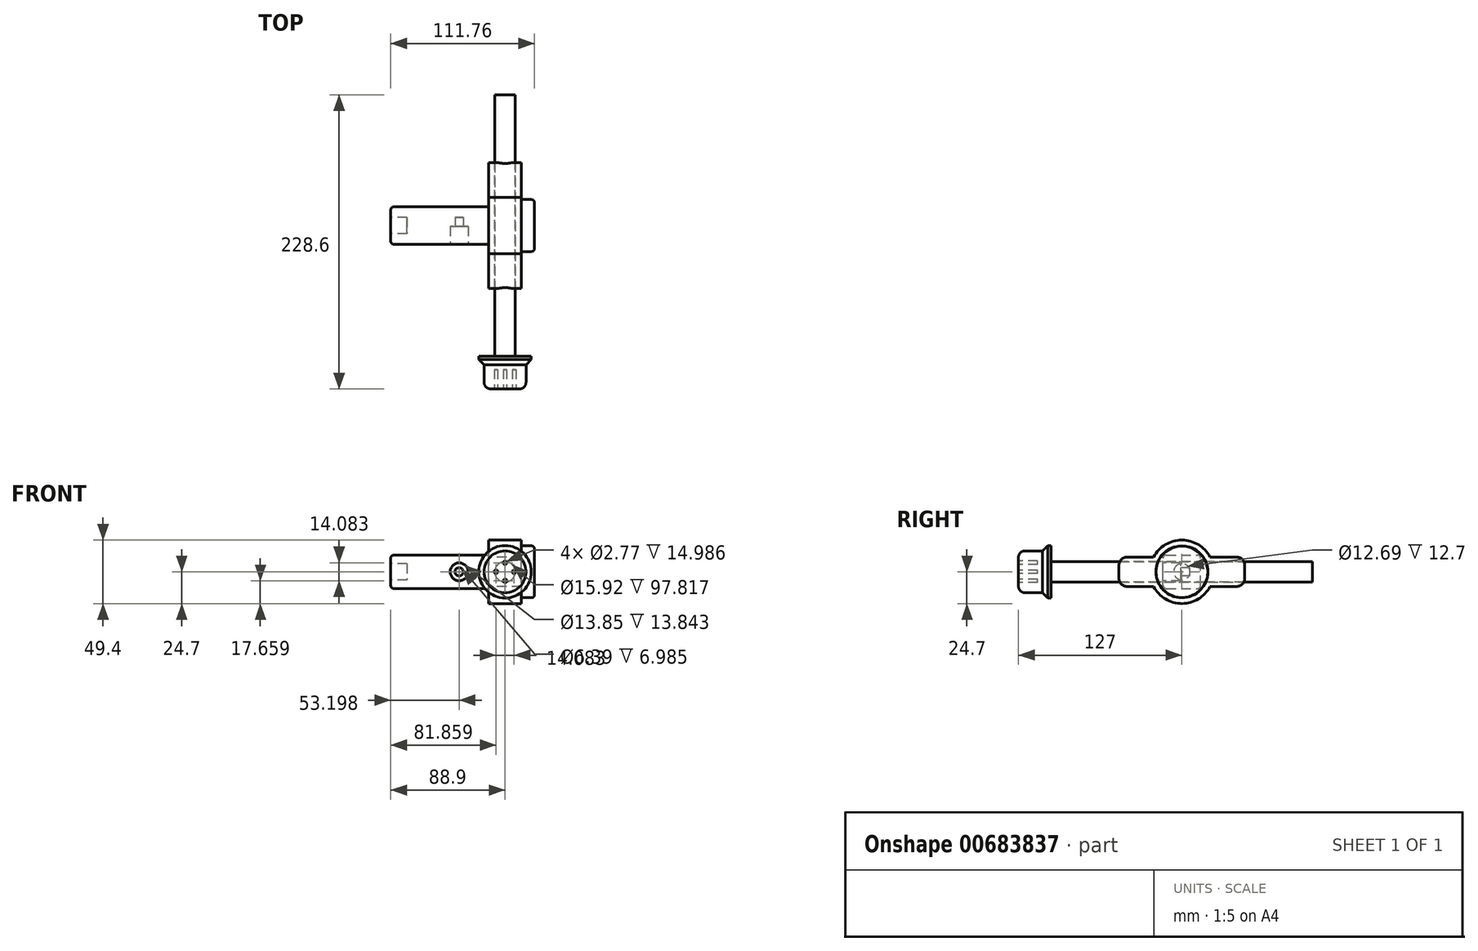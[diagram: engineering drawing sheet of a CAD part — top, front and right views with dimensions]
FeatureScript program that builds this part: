
annotation { "Feature Type Name" : "Feature", "Feature Type Description" : "" }
export const myFeature = defineFeature(function(context is Context, id is Id, definition is map)
    precondition{}
    {
        {
            var Q0;
            Q0=qCreatedBy(makeId("Right.planeOp"),FACE);
            var sketch = newSketch(context, id + "F0", { "sketchPlane" : qUnion([Q0])});
            skPoint(sketch, "E0.middle", {"position": v(0, 0) * mm});
            skPoint(sketch, "E0.left.end.orphan", {"position": v(25.79, 17.05) * mm});
            skPoint(sketch, "E0.bottom.start.orphan", {"position": v(25.79, -17.05) * mm});
            skPoint(sketch, "E0.right.start.orphan", {"position": v(-25.79, -17.05) * mm});
            skPoint(sketch, "E1.trimOffspring.end.orphan", {"position": v(-25.79, 17.05) * mm});
            skLineSegment(sketch, "E2.bottom", {"start": v(48.9, -11.44) * mm, "end": v(21.89, -11.44) * mm});
            skLineSegment(sketch, "E2.top", {"start": v(48.9, 11.44) * mm, "end": v(21.89, 11.44) * mm});
            skLineSegment(sketch, "E2.left", {"start": v(48.9, -11.44) * mm, "end": v(48.9, 11.44) * mm});
            skLineSegment(sketch, "E2.right", {"start": v(-48.9, -11.44) * mm, "end": v(-48.9, 11.44) * mm});
            skLineSegment(sketch, "E3.trimOffspring", {"start": v(-21.89, 11.44) * mm, "end": v(-48.9, 11.44) * mm});
            skLineSegment(sketch, "E4.trimOffspring", {"start": v(-21.89, -11.44) * mm, "end": v(-48.9, -11.44) * mm});
            skArc(sketch, "E5", {"start": v(21.89, 11.44) * mm, "mid": v(0, 24.7) * mm, "end": v(-21.89, 11.44) * mm});
            skArc(sketch, "E6.trimOffspring", {"start": v(-21.89, -11.44) * mm, "mid": v(0, -24.7) * mm, "end": v(21.89, -11.44) * mm});
            skSolve(sketch);
        }
        {
            var Q0;
            Q0=makeQuery(id+"F0.imprint","IMPRINT",FACE,{"disambiguationData":[TD([[makeQuery(id+"F0.imprint","IMPRINT",EDGE,{"derivedFrom":sQuery(id+"F0.wireOp",EDGE,"E2.bottom")}),-1.0]])]});
            extrude(context, id + "F1", {"entities" : qUnion([Q0]), "depth" : 12.7 * mm, "offsetDistance" : 25.4 * mm, "hasSecondDirection" : true, "secondDirectionOppositeDirection" : true, "secondDirectionDepth" : 12.7 * mm});
        }
        {
            var Q0;
            Q0=makeQuery(id+"F1.opExtrude","SWEPT_FACE",FACE,{"disambiguationData":[OSD([sQuery(id+"F0.wireOp",EDGE,"E2.right")])]});
            var sketch = newSketch(context, id + "F2", { "sketchPlane" : qUnion([Q0])});
            skCircle(sketch, "E7", {"center": v(0, 0) * mm, "radius": 7.96 * mm});
            skSolve(sketch);
        }
        {
            var Q0;
            Q0 = qSketchRegion(id + "F2", true);
            extrude(context, id + "F3", {"entities" : qUnion([Q0]), "operationType" : NewBodyOperationType.REMOVE, "oppositeDirection" : true, "depth" : 97.97 * mm, "offsetDistance" : 25.4 * mm});
        }
        {
            var Q0;
            Q0=qCreatedBy(makeId("Front.planeOp"),FACE);
            var sketch = newSketch(context, id + "F4", { "sketchPlane" : qUnion([Q0])});
            skCircle(sketch, "E8", {"center": v(0, 0) * mm, "radius": 7.96 * mm});
            skSolve(sketch);
        }
        {
            var Q0;
            Q0=makeQuery(id+"F4.imprint","IMPRINT",FACE,{"disambiguationData":[TD([[makeQuery(id+"F4.imprint","IMPRINT",EDGE,{"derivedFrom":sQuery(id+"F4.wireOp",EDGE,"E8")}),1.0]])]});
            extrude(context, id + "F5", {"entities" : qUnion([Q0]), "depth" : 101.6 * mm, "offsetDistance" : 25.4 * mm, "hasSecondDirection" : true, "secondDirectionOppositeDirection" : true, "secondDirectionDepth" : 101.6 * mm});
        }
        {
            var Q0;
            Q0=makeQuery(id+"F1.opExtrude","CAP_FACE",FACE,{"disambiguationData":[OSD([sQuery(id+"F0.wireOp",EDGE,"E2.bottom"),sQuery(id+"F0.wireOp",EDGE,"E2.top"),sQuery(id+"F0.wireOp",EDGE,"E2.left"),sQuery(id+"F0.wireOp",EDGE,"E2.right"),sQuery(id+"F0.wireOp",EDGE,"b0affe3c-eb21-476f-afb3-5162862ad022"),sQuery(id+"F0.wireOp",EDGE,"E3.trimOffspring"),sQuery(id+"F0.wireOp",EDGE,"827ddc7d-17b5-481c-bf36-fe39de4f3847.trimOffspring"),sQuery(id+"F0.wireOp",EDGE,"E4.trimOffspring")])],"isStart":false});
            var sketch = newSketch(context, id + "F6", { "sketchPlane" : qUnion([Q0])});
            skCircle(sketch, "E9", {"center": v(0, 0) * mm, "radius": 20.19 * mm});
            skSolve(sketch);
        }
        {
            var Q0;
            Q0=makeQuery(id+"F6.imprint","IMPRINT",FACE,{"disambiguationData":[TD([[makeQuery(id+"F6.imprint","IMPRINT",EDGE,{"derivedFrom":sQuery(id+"F6.wireOp",EDGE,"E9")}),1.0]])]});
            extrude(context, id + "F7", {"entities" : qUnion([Q0]), "operationType" : NewBodyOperationType.ADD, "depth" : 10.16 * mm, "offsetDistance" : 25.4 * mm});
        }
        {
            var Q0;
            Q0=makeQuery(id+"F7.opExtrude","CAP_FACE",FACE,{"disambiguationData":[OSD([sQuery(id+"F6.wireOp",EDGE,"E9")])],"isStart":false});
            fillet(context, id + "F8", {"entities" : qUnion([Q0]), "radius" : 2.54 * mm, "tangentPropagation" : true, "rho" : 0.5, "crossSection" : FilletCrossSection.CONIC, "allowEdgeOverflow" : false});
        }
        {
            var Q0;
            Q0=makeQuery(id+"F1.opExtrude","CAP_FACE",FACE,{"disambiguationData":[OSD([sQuery(id+"F0.wireOp",EDGE,"E2.bottom"),sQuery(id+"F0.wireOp",EDGE,"E2.top"),sQuery(id+"F0.wireOp",EDGE,"E2.left"),sQuery(id+"F0.wireOp",EDGE,"E2.right"),sQuery(id+"F0.wireOp",EDGE,"b0affe3c-eb21-476f-afb3-5162862ad022"),sQuery(id+"F0.wireOp",EDGE,"E3.trimOffspring"),sQuery(id+"F0.wireOp",EDGE,"827ddc7d-17b5-481c-bf36-fe39de4f3847.trimOffspring"),sQuery(id+"F0.wireOp",EDGE,"E4.trimOffspring")])],"isStart":true});
            var sketch = newSketch(context, id + "F9", { "sketchPlane" : qUnion([Q0])});
            skLineSegment(sketch, "E10.bottom", {"start": v(14.58, -13.05) * mm, "end": v(-14.58, -13.05) * mm});
            skLineSegment(sketch, "E10.top", {"start": v(14.58, 13.05) * mm, "end": v(-14.58, 13.05) * mm});
            skLineSegment(sketch, "E10.left", {"start": v(14.58, -13.05) * mm, "end": v(14.58, 13.05) * mm});
            skLineSegment(sketch, "E10.right", {"start": v(-14.58, -13.05) * mm, "end": v(-14.58, 13.05) * mm});
            skPoint(sketch, "E10.middle", {"position": v(0, 0) * mm});
            skSolve(sketch);
        }
        {
            var Q0;
            Q0=makeQuery(id+"F9.imprint","IMPRINT",FACE,{"disambiguationData":[TD([[makeQuery(id+"F9.imprint","IMPRINT",EDGE,{"derivedFrom":sQuery(id+"F9.wireOp",EDGE,"E10.bottom")}),-1.0]])]});
            extrude(context, id + "F10", {"entities" : qUnion([Q0]), "operationType" : NewBodyOperationType.ADD, "depth" : 76.2 * mm, "offsetDistance" : 25.4 * mm});
        }
        {
            var Q0;
            Q0=makeQuery(id+"F10.opExtrude","SWEPT_FACE",FACE,{"disambiguationData":[OSD([sQuery(id+"F9.wireOp",EDGE,"E10.left")])]});
            var sketch = newSketch(context, id + "F11", { "sketchPlane" : qUnion([Q0])});
            skCircle(sketch, "E11", {"center": v(-35.7, 0) * mm, "radius": 6.92 * mm});
            skCircle(sketch, "E12", {"center": v(-35.7, 0) * mm, "radius": 3.2 * mm});
            skSolve(sketch);
        }
        {
            var Q0;
            Q0=makeQuery(id+"F11.imprint","IMPRINT",FACE,{"disambiguationData":[TD([[makeQuery(id+"F11.imprint","IMPRINT",EDGE,{"derivedFrom":sQuery(id+"F11.wireOp",EDGE,"E12")}),1.0]])]});
            extrude(context, id + "F12", {"entities" : qUnion([Q0]), "operationType" : NewBodyOperationType.REMOVE, "oppositeDirection" : true, "depth" : 20.83 * mm, "offsetDistance" : 25.4 * mm});
        }
        {
            var Q0;
            Q0=makeQuery(id+"F11.imprint","IMPRINT",FACE,{"disambiguationData":[TD([[makeQuery(id+"F11.imprint","IMPRINT",EDGE,{"derivedFrom":sQuery(id+"F11.wireOp",EDGE,"E11")}),1.0]])]});
            extrude(context, id + "F13", {"entities" : qUnion([Q0]), "operationType" : NewBodyOperationType.REMOVE, "oppositeDirection" : true, "depth" : 13.84 * mm, "offsetDistance" : 25.4 * mm});
        }
        {
            var Q0;
            Q0=makeQuery(id+"F1.opExtrude","SWEPT_EDGE",EDGE,{"disambiguationData":[OSD([sQuery(id+"F0.wireOp",EDGE,"E2.top"),sQuery(id+"F0.wireOp",EDGE,"E2.left")])]});
            fillet(context, id + "F14", {"entities" : qUnion([Q0]), "radius" : 6.35 * mm, "tangentPropagation" : true, "allowEdgeOverflow" : false});
        }
        {
            var Q0;
            Q0=makeQuery(id+"F1.opExtrude","SWEPT_EDGE",EDGE,{"disambiguationData":[OSD([sQuery(id+"F0.wireOp",EDGE,"E2.bottom"),sQuery(id+"F0.wireOp",EDGE,"E2.left")])]});
            var Q1;
            Q1=makeQuery(id+"F1.opExtrude","SWEPT_EDGE",EDGE,{"disambiguationData":[OSD([sQuery(id+"F0.wireOp",EDGE,"E2.right"),sQuery(id+"F0.wireOp",EDGE,"E3.trimOffspring")])]});
            var Q2;
            Q2=makeQuery(id+"F1.opExtrude","SWEPT_EDGE",EDGE,{"disambiguationData":[OSD([sQuery(id+"F0.wireOp",EDGE,"E2.right"),sQuery(id+"F0.wireOp",EDGE,"E4.trimOffspring")])]});
            fillet(context, id + "F15", {"entities" : qUnion([Q0, Q1, Q2]), "radius" : 6.35 * mm, "tangentPropagation" : true, "allowEdgeOverflow" : false});
        }
        {
            var Q0;
            Q0=makeQuery(id+"F5.opExtrude","CAP_FACE",FACE,{"disambiguationData":[OSD([sQuery(id+"F4.wireOp",EDGE,"E8")])],"isStart":false});
            var sketch = newSketch(context, id + "F16", { "sketchPlane" : qUnion([Q0])});
            skCircle(sketch, "E13", {"center": v(0, 0) * mm, "radius": 20.41 * mm});
            skSolve(sketch);
        }
        {
            var Q0;
            Q0 = qSketchRegion(id + "F16", true);
            extrude(context, id + "F17", {"entities" : qUnion([Q0]), "operationType" : NewBodyOperationType.ADD, "depth" : 7.62 * mm, "offsetDistance" : 25.4 * mm});
        }
        {
            var Q0;
            Q0=makeQuery(id+"F17.opExtrude","CAP_FACE",FACE,{"disambiguationData":[OSD([sQuery(id+"F16.wireOp",EDGE,"E13")])],"isStart":false});
            var sketch = newSketch(context, id + "F18", { "sketchPlane" : qUnion([Q0])});
            skCircle(sketch, "E14", {"center": v(0, 0) * mm, "radius": 16.3 * mm});
            skSolve(sketch);
        }
        {
            var Q0;
            Q0 = qSketchRegion(id + "F18", true);
            extrude(context, id + "F19", {"entities" : qUnion([Q0]), "operationType" : NewBodyOperationType.ADD, "depth" : 17.78 * mm, "offsetDistance" : 25.4 * mm});
        }
        {
            var Q0;
            Q0=makeQuery(id+"F19.opExtrude","CAP_EDGE",EDGE,{"disambiguationData":[OSD([sQuery(id+"F18.wireOp",EDGE,"E14")])],"isStart":false});
            fillet(context, id + "F20", {"entities" : qUnion([Q0]), "radius" : 5.08 * mm, "tangentPropagation" : true, "allowEdgeOverflow" : false});
        }
        {
            var Q0;
            Q0=makeQuery(id+"F17.opExtrude","CAP_EDGE",EDGE,{"disambiguationData":[OSD([sQuery(id+"F16.wireOp",EDGE,"E13")])],"isStart":false});
            chamfer(context, id + "F21", {"entities" : qUnion([Q0]), "width" : 5.08 * mm, "tangentPropagation" : true});
        }
        {
            var Q0;
            Q0=makeQuery(id+"F19.opExtrude","CAP_FACE",FACE,{"disambiguationData":[OSD([sQuery(id+"F18.wireOp",EDGE,"E14")])],"isStart":false});
            var sketch = newSketch(context, id + "F22", { "sketchPlane" : qUnion([Q0])});
            skCircle(sketch, "E15", {"center": v(0, 7.04) * mm, "radius": 1.38 * mm});
            skCircle(sketch, "E16.1.0", {"center": v(7.04, 0) * mm, "radius": 1.38 * mm});
            skCircle(sketch, "E16.2.0", {"center": v(0, -7.04) * mm, "radius": 1.38 * mm});
            skCircle(sketch, "E16.3.0", {"center": v(-7.04, 0) * mm, "radius": 1.38 * mm});
            skPoint(sketch, "E16.center", {"position": v(0, 0) * mm});
            skLineSegment(sketch, "E16.anchor1", {"start": v(0, 0) * mm, "end": v(0, 7.04) * mm, "construction": true});
            skLineSegment(sketch, "E16.anchor2", {"start": v(0, 0) * mm, "end": v(-7.04, 0) * mm, "construction": true});
            skSolve(sketch);
        }
        {
            var Q0;
            Q0 = qSketchRegion(id + "F22", true);
            extrude(context, id + "F23", {"entities" : qUnion([Q0]), "operationType" : NewBodyOperationType.REMOVE, "oppositeDirection" : true, "depth" : 15 * mm, "offsetDistance" : 25.4 * mm});
        }
        {
            var Q0;
            Q0=makeQuery(id+"F10.opExtrude","SWEPT_EDGE",EDGE,{"disambiguationData":[OSD([sQuery(id+"F9.wireOp",EDGE,"E10.top"),sQuery(id+"F9.wireOp",EDGE,"E10.right")])]});
            var Q1;
            Q1=makeQuery(id+"F10.opExtrude","SWEPT_EDGE",EDGE,{"disambiguationData":[OSD([sQuery(id+"F9.wireOp",EDGE,"E10.bottom"),sQuery(id+"F9.wireOp",EDGE,"E10.right")])]});
            var Q2;
            Q2=makeQuery(id+"F10.opExtrude","SWEPT_EDGE",EDGE,{"disambiguationData":[OSD([sQuery(id+"F9.wireOp",EDGE,"E10.top"),sQuery(id+"F9.wireOp",EDGE,"E10.left")])]});
            var Q3;
            Q3=makeQuery(id+"F10.opExtrude","SWEPT_EDGE",EDGE,{"disambiguationData":[OSD([sQuery(id+"F9.wireOp",EDGE,"E10.bottom"),sQuery(id+"F9.wireOp",EDGE,"E10.left")])]});
            fillet(context, id + "F24", {"entities" : qUnion([Q0, Q1, Q2, Q3]), "radius" : 2.54 * mm, "tangentPropagation" : true, "allowEdgeOverflow" : false});
        }
        {
            var Q0;
            Q0=makeQuery(id+"F10.opExtrude","CAP_EDGE",EDGE,{"disambiguationData":[OSD([sQuery(id+"F9.wireOp",EDGE,"E10.top")])],"isStart":false});
            var Q1;
            Q1=makeQuery(id+"F10.opExtrude","CAP_EDGE",EDGE,{"disambiguationData":[OSD([sQuery(id+"F9.wireOp",EDGE,"E10.bottom")])],"isStart":false});
            var Q2;
            Q2=makeQuery(id+"F10.opExtrude","CAP_EDGE",EDGE,{"disambiguationData":[OSD([sQuery(id+"F9.wireOp",EDGE,"E10.left")])],"isStart":false});
            var Q3;
            Q3=makeQuery(id+"F10.opExtrude","CAP_EDGE",EDGE,{"disambiguationData":[OSD([sQuery(id+"F9.wireOp",EDGE,"E10.right")])],"isStart":false});
            fillet(context, id + "F25", {"entities" : qUnion([Q0, Q1, Q2, Q3]), "radius" : 2.54 * mm, "tangentPropagation" : true, "allowEdgeOverflow" : false});
        }
        {
            var Q0;
            Q0=makeQuery(id+"F10.opExtrude","CAP_FACE",FACE,{"disambiguationData":[OSD([sQuery(id+"F9.wireOp",EDGE,"E10.bottom"),sQuery(id+"F9.wireOp",EDGE,"E10.top"),sQuery(id+"F9.wireOp",EDGE,"E10.left"),sQuery(id+"F9.wireOp",EDGE,"E10.right")])],"isStart":false});
            var sketch = newSketch(context, id + "F26", { "sketchPlane" : qUnion([Q0])});
            skCircle(sketch, "E17", {"center": v(0, 0) * mm, "radius": 6.35 * mm});
            skSolve(sketch);
        }
        {
            var Q0;
            Q0 = qSketchRegion(id + "F26", true);
            extrude(context, id + "F27", {"entities" : qUnion([Q0]), "operationType" : NewBodyOperationType.REMOVE, "oppositeDirection" : true, "depth" : 12.7 * mm, "offsetDistance" : 25.4 * mm});
        }
    });
